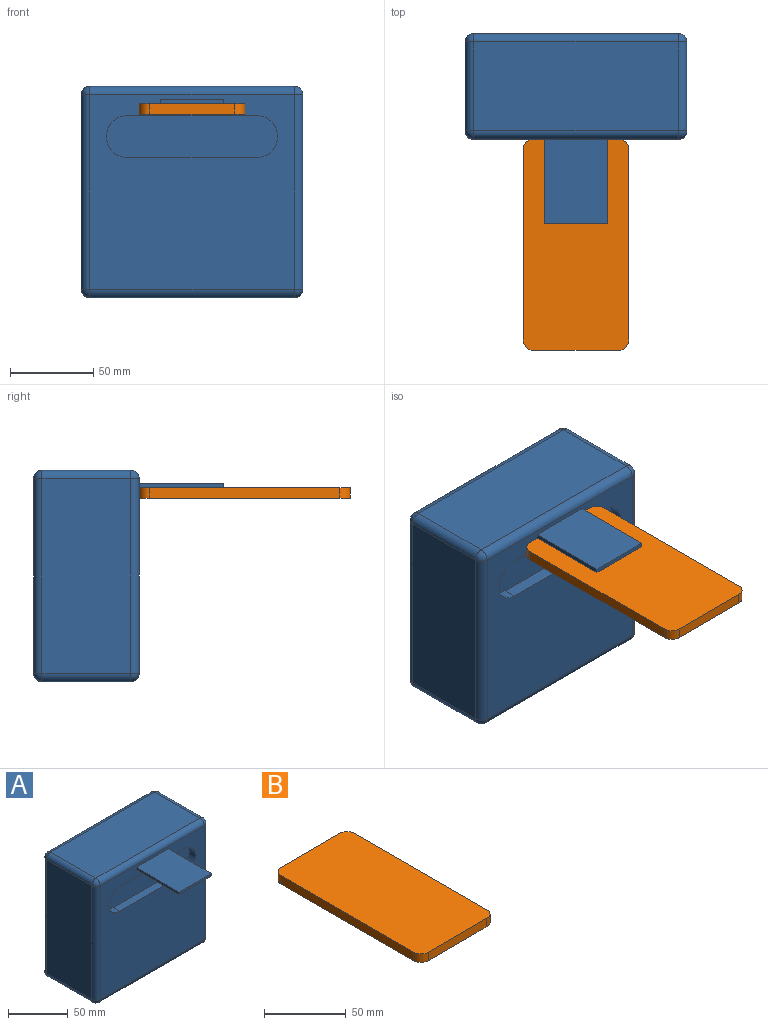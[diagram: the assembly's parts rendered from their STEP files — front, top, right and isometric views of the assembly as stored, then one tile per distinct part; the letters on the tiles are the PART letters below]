
ASSEMBLY  parts=2 mates=1
PART A: 41 faces, bbox 133.4x114.3x127 mm
  f0: plane 116.84x53.34mm, normal (1,0,0), area 6232.2mm2, adj f7,f12,f17,f24
  f1: plane 123.19x53.34mm, normal (0,0,1), area 6571mm2, adj f10,f15,f21,f24
  f2: plane 116.84x53.34mm, normal (-1,0,0), area 6232.2mm2, adj f6,f8,f14,f21
  f3: plane 123.19x53.34mm, normal (0,0,-1), area 6571mm2, adj f6,f7,f11,f18
  f4: plane 123.19x116.84mm, normal (0,-1,0), area 11780.4mm2, adj f8,f10,f11,f12,f26,f27,f28,f29
  f5: plane 123.19x116.84mm, normal (0,1,0), area 14393.5mm2, adj f14,f15,f17,f18
  f6: cylinder r=5.08mm len=53.34mm, axis (0,-1,0), area 425.6mm2, adj f2,f3,f9,f16
  f7: cylinder r=5.08mm len=53.34mm, axis (0,1,0), area 425.6mm2, adj f0,f3,f13,f19
  f8: cylinder r=5.08mm len=116.84mm, axis (0,0,1), area 932.3mm2, adj f2,f4,f9,f22
  f9: sphere r=5.08mm, area 40.5mm2, adj f6,f8,f11
  f10: cylinder r=5.08mm len=123.19mm, axis (1,0,0), area 983mm2, adj f1,f4,f22,f25
  f11: cylinder r=5.08mm len=123.19mm, axis (-1,0,0), area 983mm2, adj f3,f4,f9,f13
  f12: cylinder r=5.08mm len=116.84mm, axis (0,0,-1), area 932.3mm2, adj f0,f4,f13,f25
  f13: sphere r=5.08mm, area 40.5mm2, adj f7,f11,f12
  f14: cylinder r=5.08mm len=116.84mm, axis (0,0,-1), area 932.3mm2, adj f2,f5,f16,f20
  f15: cylinder r=5.08mm len=123.19mm, axis (-1,0,0), area 983mm2, adj f1,f5,f20,f23
  f16: sphere r=5.08mm, area 40.5mm2, adj f6,f14,f18
  f17: cylinder r=5.08mm len=116.84mm, axis (0,0,1), area 932.3mm2, adj f0,f5,f19,f23
  f18: cylinder r=5.08mm len=123.19mm, axis (1,0,0), area 983mm2, adj f3,f5,f16,f19
  f19: sphere r=5.08mm, area 40.5mm2, adj f7,f17,f18
  f20: sphere r=5.08mm, area 40.5mm2, adj f14,f15,f21
  f21: cylinder r=5.08mm len=53.34mm, axis (0,1,0), area 425.6mm2, adj f1,f2,f20,f22
  f22: sphere r=5.08mm, area 40.5mm2, adj f8,f10,f21
  f23: sphere r=5.08mm, area 40.5mm2, adj f15,f17,f24
  f24: cylinder r=5.08mm len=53.34mm, axis (0,-1,0), area 425.6mm2, adj f0,f1,f23,f25
  f25: sphere r=5.08mm, area 40.5mm2, adj f10,f12,f24
  f26: plane 12.7x5.08mm, normal (0,0,-1), area 64.5mm2, adj f4,f27,f29,f30
  f27: plane 5.08x3.3mm, normal (1,0,0), area 16.8mm2, adj f4,f26,f28,f30
  f28: plane 12.7x5.08mm, normal (0,0,1), area 64.5mm2, adj f4,f27,f29,f30
  f29: plane 5.08x3.3mm, normal (-1,0,0), area 16.8mm2, adj f4,f26,f28,f30
  f30: plane 12.7x3.3mm, normal (0,-1,0), area 41.9mm2, adj f26,f27,f28,f29
  f31: cylinder r=12.7mm len=25.4mm, axis (0,-1,0), area 304mm2, adj f4,f32,f34,f35
  f32: plane 77.47x7.62mm, normal (0,0,1), area 590.3mm2, adj f4,f31,f33,f35
  f33: cylinder r=12.7mm len=25.4mm, axis (0,-1,0), area 304mm2, adj f4,f32,f34,f35
  f34: plane 77.47x7.62mm, normal (0,0,-1), area 590.3mm2, adj f4,f31,f33,f35
  f35: plane 102.87x25.4mm, normal (0,-1,0), area 2474.4mm2, adj f31,f32,f33,f34
  f36: plane 50.8x2.54mm, normal (1,0,0), area 129mm2, adj f4,f37,f39,f40
  f37: plane 50.8x38.1mm, normal (0,0,1), area 1935.5mm2, adj f4,f36,f38,f40
  f38: plane 50.8x2.54mm, normal (-1,0,0), area 129mm2, adj f4,f37,f39,f40
  f39: plane 50.8x38.1mm, normal (0,0,-1), area 1935.5mm2, adj f4,f36,f38,f40
  f40: plane 38.1x2.54mm, normal (0,-1,0), area 96.8mm2, adj f36,f37,f38,f39
PART B: 15 faces, bbox 63.5x127x6.4 mm
  f0: plane 50.8x6.35mm, normal (0,1,0), area 290.3mm2, adj f1,f7,f8,f9,f10,f11,f12,f13
  f1: cylinder r=6.35mm len=6.35mm, axis (0,0,-1), area 63.3mm2, adj f0,f2,f8,f9
  f2: plane 114.3x6.35mm, normal (-1,0,0), area 725.8mm2, adj f1,f3,f8,f9
  f3: cylinder r=6.35mm len=6.35mm, axis (0,0,-1), area 63.3mm2, adj f2,f4,f8,f9
  f4: plane 50.8x6.35mm, normal (0,-1,0), area 322.6mm2, adj f3,f5,f8,f9
  f5: cylinder r=6.35mm len=6.35mm, axis (0,0,-1), area 63.3mm2, adj f4,f6,f8,f9
  f6: plane 114.3x6.35mm, normal (1,0,0), area 725.8mm2, adj f5,f7,f8,f9
  f7: cylinder r=6.35mm len=6.35mm, axis (0,0,-1), area 63.3mm2, adj f0,f6,f8,f9
  f8: plane 127x63.5mm, normal (0,0,1), area 8029.9mm2, adj f0,f1,f2,f3,f4,f5,f6,f7
  f9: plane 127x63.5mm, normal (0,0,-1), area 8029.9mm2, adj f0,f1,f2,f3,f4,f5,f6,f7
  f10: plane 12.7x3.81mm, normal (0,0,-1), area 48.4mm2, adj f0,f11,f13,f14
  f11: plane 3.81x2.54mm, normal (-1,0,0), area 9.7mm2, adj f0,f10,f12,f14
  f12: plane 12.7x3.81mm, normal (0,0,1), area 48.4mm2, adj f0,f11,f13,f14
  f13: plane 3.81x2.54mm, normal (1,0,0), area 9.7mm2, adj f0,f10,f12,f14
  f14: plane 12.7x2.54mm, normal (0,1,0), area 32.3mm2, adj f10,f11,f12,f13
PLACE A t=(-120.04,20.72,14.51)mm
PLACE B rot(axis=(0.96,0.16,0.23),0deg) t=(-120.04,-106.28,61.26)mm
MATE slider A.f30 <-> B.f0  axis (0,-1,0) through (-120.04,-47.86,64.42)mm
